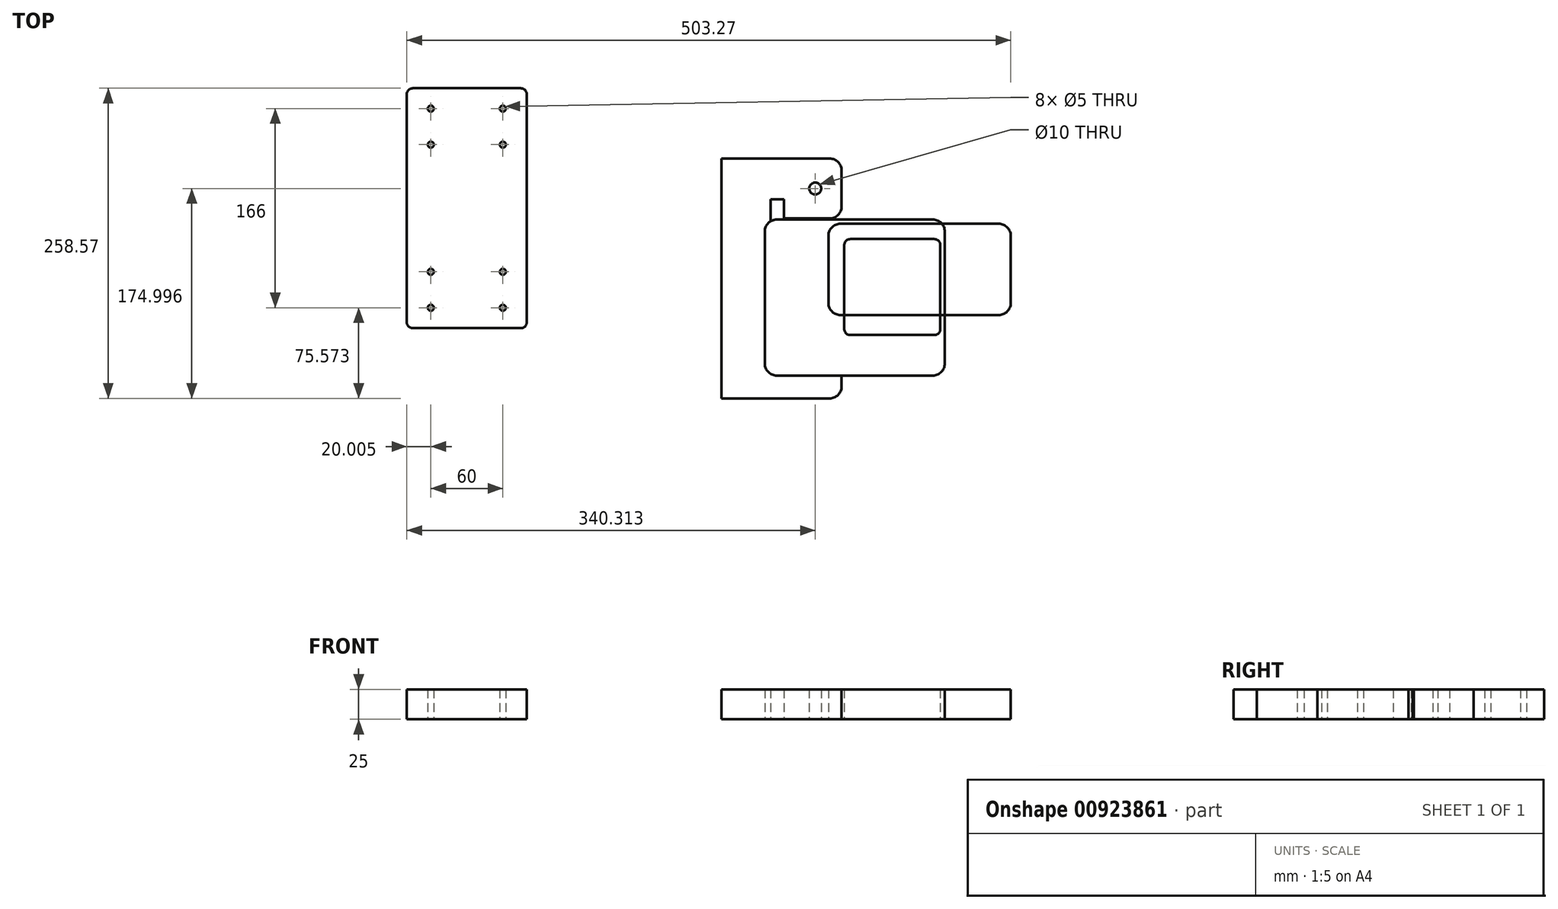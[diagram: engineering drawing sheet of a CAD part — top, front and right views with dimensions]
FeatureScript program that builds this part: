
annotation { "Feature Type Name" : "Feature", "Feature Type Description" : "" }
export const myFeature = defineFeature(function(context is Context, id is Id, definition is map)
    precondition{}
    {
        {
            var Q0;
            Q0=qCreatedBy(makeId("Top.planeOp"),FACE);
            var sketch = newSketch(context, id + "F0", { "sketchPlane" : qUnion([Q0])});
            skLineSegment(sketch, "E0.bottom", {"start": v(-167.24, 75.97) * mm, "end": v(-37.24, 75.97) * mm});
            skLineSegment(sketch, "E0.top", {"start": v(-167.24, -54.03) * mm, "end": v(-37.24, -54.03) * mm});
            skLineSegment(sketch, "E0.left", {"start": v(-177.24, 65.97) * mm, "end": v(-177.24, -44.03) * mm});
            skLineSegment(sketch, "E0.right", {"start": v(-27.24, 65.97) * mm, "end": v(-27.24, -44.03) * mm});
            skPoint(sketch, "E1.visualSharp", {"position": v(-177.24, 75.97) * mm});
            skArc(sketch, "E1.filletArc", {"start": v(-167.24, 75.97) * mm, "mid": v(-174.3, 73.04) * mm, "end": v(-177.24, 65.97) * mm});
            skPoint(sketch, "E2.visualSharp", {"position": v(-27.24, 75.97) * mm});
            skArc(sketch, "E2.filletArc", {"start": v(-27.24, 65.97) * mm, "mid": v(-30.17, 73.04) * mm, "end": v(-37.24, 75.97) * mm});
            skPoint(sketch, "E3.visualSharp", {"position": v(-177.24, -54.03) * mm});
            skArc(sketch, "E3.filletArc", {"start": v(-177.24, -44.03) * mm, "mid": v(-174.3, -51.1) * mm, "end": v(-167.24, -54.03) * mm});
            skPoint(sketch, "E4.visualSharp", {"position": v(-27.24, -54.03) * mm});
            skArc(sketch, "E4.filletArc", {"start": v(-37.24, -54.03) * mm, "mid": v(-30.17, -51.1) * mm, "end": v(-27.24, -44.03) * mm});
            skSolve(sketch);
        }
        {
            var Q0;
            Q0=qCreatedBy(makeId("Top.planeOp"),FACE);
            var sketch = newSketch(context, id + "F1", { "sketchPlane" : qUnion([Q0])});
            skLineSegment(sketch, "E5.bottom", {"start": v(-470.5, 185.44) * mm, "end": v(-380.5, 185.44) * mm});
            skLineSegment(sketch, "E5.top", {"start": v(-470.5, -14.56) * mm, "end": v(-380.5, -14.56) * mm});
            skLineSegment(sketch, "E5.left", {"start": v(-475.5, 180.44) * mm, "end": v(-475.5, -9.56) * mm});
            skLineSegment(sketch, "E5.right", {"start": v(-375.5, 180.44) * mm, "end": v(-375.5, -9.56) * mm});
            skCircle(sketch, "E6", {"center": v(-455.5, 168.44) * mm, "radius": 2.5 * mm});
            skCircle(sketch, "E7", {"center": v(-455.5, 138.44) * mm, "radius": 2.5 * mm});
            skCircle(sketch, "E8", {"center": v(-455.5, 32.44) * mm, "radius": 2.5 * mm});
            skCircle(sketch, "E9", {"center": v(-455.5, 2.44) * mm, "radius": 2.5 * mm});
            skCircle(sketch, "E10", {"center": v(-395.5, 2.44) * mm, "radius": 2.5 * mm});
            skCircle(sketch, "E11", {"center": v(-395.5, 32.44) * mm, "radius": 2.5 * mm});
            skCircle(sketch, "E12", {"center": v(-395.5, 138.44) * mm, "radius": 2.5 * mm});
            skCircle(sketch, "E13", {"center": v(-395.5, 168.44) * mm, "radius": 2.5 * mm});
            skPoint(sketch, "E14.visualSharp", {"position": v(-475.5, 185.44) * mm});
            skArc(sketch, "E14.filletArc", {"start": v(-470.5, 185.44) * mm, "mid": v(-474.03, 183.98) * mm, "end": v(-475.5, 180.44) * mm});
            skPoint(sketch, "E15.visualSharp", {"position": v(-375.5, 185.44) * mm});
            skArc(sketch, "E15.filletArc", {"start": v(-375.5, 180.44) * mm, "mid": v(-376.96, 183.98) * mm, "end": v(-380.5, 185.44) * mm});
            skPoint(sketch, "E16.visualSharp", {"position": v(-375.5, -14.56) * mm});
            skArc(sketch, "E16.filletArc", {"start": v(-380.5, -14.56) * mm, "mid": v(-376.96, -13.1) * mm, "end": v(-375.5, -9.56) * mm});
            skPoint(sketch, "E17.visualSharp", {"position": v(-475.5, -14.56) * mm});
            skArc(sketch, "E17.filletArc", {"start": v(-475.5, -9.56) * mm, "mid": v(-474.03, -13.1) * mm, "end": v(-470.5, -14.56) * mm});
            skSolve(sketch);
        }
        {
            var Q0;
            Q0 = qSketchRegion(id + "F1", true);
            extrude(context, id + "F2", {"entities" : qUnion([Q0]), "depth" : 25 * mm, "offsetDistance" : 25 * mm});
        }
        {
            var Q0;
            Q0=qCreatedBy(makeId("Top.planeOp"),FACE);
            var sketch = newSketch(context, id + "F3", { "sketchPlane" : qUnion([Q0])});
            skLineSegment(sketch, "E18", {"start": v(-213.19, 126.87) * mm, "end": v(-123.19, 126.87) * mm});
            skLineSegment(sketch, "E19", {"start": v(-113.19, 116.87) * mm, "end": v(-113.19, 86.87) * mm});
            skLineSegment(sketch, "E20", {"start": v(-123.19, 76.87) * mm, "end": v(-161.19, 76.87) * mm});
            skLineSegment(sketch, "E21", {"start": v(-161.19, 76.87) * mm, "end": v(-161.19, 92.87) * mm});
            skLineSegment(sketch, "E22", {"start": v(-161.19, 92.87) * mm, "end": v(-172.19, 92.87) * mm});
            skLineSegment(sketch, "E23", {"start": v(-172.19, 92.87) * mm, "end": v(-172.19, -39.13) * mm});
            skLineSegment(sketch, "E24", {"start": v(-172.19, -39.13) * mm, "end": v(-161.19, -39.13) * mm});
            skLineSegment(sketch, "E25", {"start": v(-161.19, -39.13) * mm, "end": v(-161.19, -23.13) * mm});
            skLineSegment(sketch, "E26", {"start": v(-161.19, -23.13) * mm, "end": v(-123.19, -23.13) * mm});
            skLineSegment(sketch, "E27", {"start": v(-113.19, -33.13) * mm, "end": v(-113.19, -63.13) * mm});
            skLineSegment(sketch, "E28", {"start": v(-123.19, -73.13) * mm, "end": v(-213.19, -73.13) * mm});
            skLineSegment(sketch, "E29", {"start": v(-213.19, -73.13) * mm, "end": v(-213.19, 126.87) * mm});
            skPoint(sketch, "E30.visualSharp", {"position": v(-113.19, 126.87) * mm});
            skArc(sketch, "E30.filletArc", {"start": v(-113.19, 116.87) * mm, "mid": v(-116.12, 123.94) * mm, "end": v(-123.19, 126.87) * mm});
            skPoint(sketch, "E31.visualSharp", {"position": v(-113.19, 76.87) * mm});
            skArc(sketch, "E31.filletArc", {"start": v(-123.19, 76.87) * mm, "mid": v(-116.12, 79.8) * mm, "end": v(-113.19, 86.87) * mm});
            skPoint(sketch, "E32.visualSharp", {"position": v(-113.19, -23.13) * mm});
            skArc(sketch, "E32.filletArc", {"start": v(-113.19, -33.13) * mm, "mid": v(-116.12, -26.06) * mm, "end": v(-123.19, -23.13) * mm});
            skPoint(sketch, "E33.visualSharp", {"position": v(-113.19, -73.13) * mm});
            skArc(sketch, "E33.filletArc", {"start": v(-123.19, -73.13) * mm, "mid": v(-116.12, -70.2) * mm, "end": v(-113.19, -63.13) * mm});
            skCircle(sketch, "E34", {"center": v(-135.19, 101.87) * mm, "radius": 5 * mm});
            skSolve(sketch);
        }
        {
            var Q0;
            Q0 = qSketchRegion(id + "F3", true);
            extrude(context, id + "F4", {"entities" : qUnion([Q0]), "depth" : 25 * mm, "offsetDistance" : 25 * mm});
        }
        {
            var Q0;
            Q0 = qSketchRegion(id + "F0", true);
            extrude(context, id + "F5", {"entities" : qUnion([Q0]), "operationType" : NewBodyOperationType.ADD, "depth" : 25 * mm, "offsetDistance" : 25 * mm});
        }
        {
            var Q0;
            Q0 = qSketchRegion(id + "F0", true);
            extrude(context, id + "F6", {"entities" : qUnion([Q0]), "depth" : 25 * mm, "offsetDistance" : 25 * mm});
        }
        {
            var Q0;
            Q0=qCreatedBy(makeId("Top.planeOp"),FACE);
            var sketch = newSketch(context, id + "F7", { "sketchPlane" : qUnion([Q0])});
            skLineSegment(sketch, "E35.bottom", {"start": v(-105.94, 59.7) * mm, "end": v(-35.94, 59.7) * mm});
            skLineSegment(sketch, "E35.top", {"start": v(-105.94, -20.3) * mm, "end": v(-35.94, -20.3) * mm});
            skLineSegment(sketch, "E35.left", {"start": v(-110.94, 54.7) * mm, "end": v(-110.94, -15.3) * mm});
            skLineSegment(sketch, "E35.right", {"start": v(-30.94, 54.7) * mm, "end": v(-30.94, -15.3) * mm});
            skPoint(sketch, "E36.visualSharp", {"position": v(-110.94, 59.7) * mm});
            skArc(sketch, "E36.filletArc", {"start": v(-105.94, 59.7) * mm, "mid": v(-109.47, 58.23) * mm, "end": v(-110.94, 54.7) * mm});
            skPoint(sketch, "E37.visualSharp", {"position": v(-30.94, 59.7) * mm});
            skArc(sketch, "E37.filletArc", {"start": v(-30.94, 54.7) * mm, "mid": v(-32.4, 58.23) * mm, "end": v(-35.94, 59.7) * mm});
            skPoint(sketch, "E38.visualSharp", {"position": v(-30.94, -20.3) * mm});
            skArc(sketch, "E38.filletArc", {"start": v(-35.94, -20.3) * mm, "mid": v(-32.4, -18.84) * mm, "end": v(-30.94, -15.3) * mm});
            skPoint(sketch, "E39.visualSharp", {"position": v(-110.94, -20.3) * mm});
            skArc(sketch, "E39.filletArc", {"start": v(-110.94, -15.3) * mm, "mid": v(-109.47, -18.84) * mm, "end": v(-105.94, -20.3) * mm});
            skSolve(sketch);
        }
        {
            var Q0;
            Q0 = qSketchRegion(id + "F7", true);
            extrude(context, id + "F8", {"entities" : qUnion([Q0]), "depth" : 25 * mm, "offsetDistance" : 25 * mm});
        }
        {
            var Q0;
            Q0=qCreatedBy(makeId("Top.planeOp"),FACE);
            var sketch = newSketch(context, id + "F9", { "sketchPlane" : qUnion([Q0])});
            skLineSegment(sketch, "E40.bottom", {"start": v(-114.23, 72.44) * mm, "end": v(17.77, 72.44) * mm});
            skLineSegment(sketch, "E40.top", {"start": v(-114.23, -3.56) * mm, "end": v(17.77, -3.56) * mm});
            skLineSegment(sketch, "E40.left", {"start": v(-124.23, 62.44) * mm, "end": v(-124.23, 6.44) * mm});
            skLineSegment(sketch, "E40.right", {"start": v(27.77, 62.44) * mm, "end": v(27.77, 6.44) * mm});
            skPoint(sketch, "E41.visualSharp", {"position": v(-124.23, 72.44) * mm});
            skArc(sketch, "E41.filletArc", {"start": v(-114.23, 72.44) * mm, "mid": v(-121.3, 69.5) * mm, "end": v(-124.23, 62.44) * mm});
            skPoint(sketch, "E42.visualSharp", {"position": v(27.77, 72.44) * mm});
            skArc(sketch, "E42.filletArc", {"start": v(27.77, 62.44) * mm, "mid": v(24.85, 69.5) * mm, "end": v(17.77, 72.44) * mm});
            skPoint(sketch, "E43.visualSharp", {"position": v(27.77, -3.56) * mm});
            skArc(sketch, "E43.filletArc", {"start": v(17.77, -3.56) * mm, "mid": v(24.85, -0.64) * mm, "end": v(27.77, 6.44) * mm});
            skPoint(sketch, "E44.visualSharp", {"position": v(-124.23, -3.56) * mm});
            skArc(sketch, "E44.filletArc", {"start": v(-124.23, 6.44) * mm, "mid": v(-121.3, -0.64) * mm, "end": v(-114.23, -3.56) * mm});
            skSolve(sketch);
        }
        {
            var Q0;
            Q0 = qSketchRegion(id + "F9", true);
            extrude(context, id + "F10", {"entities" : qUnion([Q0]), "depth" : 25 * mm, "offsetDistance" : 25 * mm});
        }
    });
